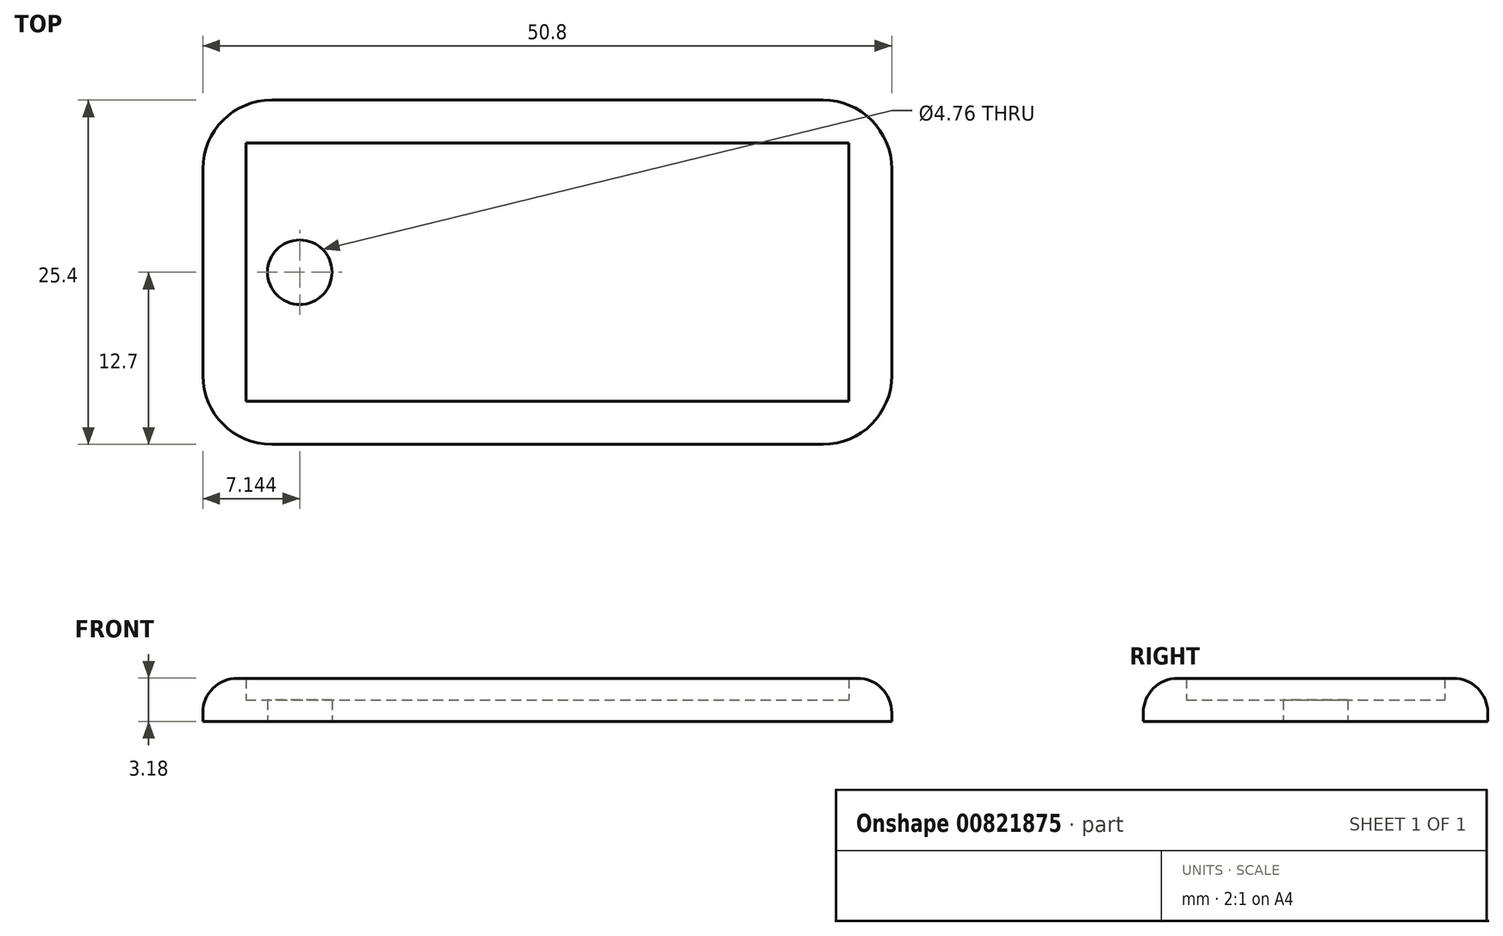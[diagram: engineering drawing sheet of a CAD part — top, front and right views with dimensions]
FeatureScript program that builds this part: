
annotation { "Feature Type Name" : "Feature", "Feature Type Description" : "" }
export const myFeature = defineFeature(function(context is Context, id is Id, definition is map)
    precondition{}
    {
        {
            var Q0;
            Q0=qCreatedBy(makeId("Top.planeOp"),FACE);
            var sketch = newSketch(context, id + "F0", { "sketchPlane" : qUnion([Q0])});
            skLineSegment(sketch, "E0.bottom", {"start": v(0, 0) * mm, "end": v(50.8, 0) * mm});
            skLineSegment(sketch, "E0.top", {"start": v(0, 25.4) * mm, "end": v(50.8, 25.4) * mm});
            skLineSegment(sketch, "E0.left", {"start": v(0, 0) * mm, "end": v(0, 25.4) * mm});
            skLineSegment(sketch, "E0.right", {"start": v(50.8, 0) * mm, "end": v(50.8, 25.4) * mm});
            skPoint(sketch, "E1.centerSnap0", {"position": v(0, 12.7) * mm});
            skLineSegment(sketch, "E2.0", {"start": v(3.18, 3.18) * mm, "end": v(47.63, 3.18) * mm});
            skLineSegment(sketch, "E2.1", {"start": v(3.17, 3.18) * mm, "end": v(3.17, 22.23) * mm});
            skLineSegment(sketch, "E2.2", {"start": v(3.17, 22.23) * mm, "end": v(47.63, 22.23) * mm});
            skLineSegment(sketch, "E2.3", {"start": v(47.63, 3.18) * mm, "end": v(47.63, 22.23) * mm});
            skPoint(sketch, "E1.center.orphan", {"position": v(3.8, 12.7) * mm});
            skCircle(sketch, "E3", {"center": v(7.14, 12.7) * mm, "radius": 2.38 * mm});
            skSolve(sketch);
        }
        {
            var Q0;
            {var subQ4=sQuery(id+"F0.wireOp",EDGE,"E2.0");Q0=makeQuery(id+"F0.imprint","IMPRINT",FACE,{"disambiguationData":[TD([[makeQuery(id+"F0.imprint","IMPRINT",EDGE,{"derivedFrom":subQ4}),1.0]])]});}
            extrude(context, id + "F1", {"entities" : qUnion([Q0]), "depth" : 1.59 * mm, "offsetDistance" : 25.4 * mm});
        }
        {
            var Q0;
            Q0=makeQuery(id+"F0.imprint","IMPRINT",FACE,{"disambiguationData":[TD([[makeQuery(id+"F0.imprint","IMPRINT",EDGE,{"derivedFrom":sQuery(id+"F0.wireOp",EDGE,"E0.bottom")}),1.0]])]});
            extrude(context, id + "F2", {"entities" : qUnion([Q0]), "operationType" : NewBodyOperationType.ADD, "depth" : 3.17 * mm, "offsetDistance" : 25.4 * mm});
        }
        {
            var Q0;
            Q0=makeQuery(id+"F2.opExtrude","SWEPT_EDGE",EDGE,{"disambiguationData":[OSD([sQuery(id+"F0.wireOp",EDGE,"E0.bottom"),sQuery(id+"F0.wireOp",EDGE,"E0.right")])]});
            var Q1;
            Q1=makeQuery(id+"F2.opExtrude","SWEPT_EDGE",EDGE,{"disambiguationData":[OSD([sQuery(id+"F0.wireOp",EDGE,"E0.bottom"),sQuery(id+"F0.wireOp",EDGE,"E0.left")])]});
            var Q2;
            Q2=makeQuery(id+"F2.opExtrude","SWEPT_EDGE",EDGE,{"disambiguationData":[OSD([sQuery(id+"F0.wireOp",EDGE,"E0.top"),sQuery(id+"F0.wireOp",EDGE,"E0.right")])]});
            var Q3;
            Q3=makeQuery(id+"F2.opExtrude","SWEPT_EDGE",EDGE,{"disambiguationData":[OSD([sQuery(id+"F0.wireOp",EDGE,"E0.top"),sQuery(id+"F0.wireOp",EDGE,"E0.left")])]});
            fillet(context, id + "F3", {"entities" : qUnion([Q0, Q1, Q2, Q3]), "radius" : 5.08 * mm, "tangentPropagation" : true, "allowEdgeOverflow" : false});
        }
        {
            var Q0;
            Q0=makeQuery(id+"F2.opExtrude","CAP_EDGE",EDGE,{"disambiguationData":[OSD([sQuery(id+"F0.wireOp",EDGE,"E0.bottom")])],"isStart":false});
            fillet(context, id + "F4", {"entities" : qUnion([Q0]), "radius" : 2.54 * mm, "tangentPropagation" : true, "allowEdgeOverflow" : false});
        }
        {
            var Q0;
            Q0=qCreatedBy(makeId("Top.planeOp"),FACE);
            var sketch = newSketch(context, id + "F5", { "sketchPlane" : qUnion([Q0])});
            skText(sketch, "E4", { "text": "Amanda", "fontName": "OpenSans-Bold.ttf"});
            const initialGuessF5  = {"E4": [0.00918, 0.0093, 1, 0, 0.0066]};
            skSetInitialGuess(sketch, initialGuessF5);
            skSolve(sketch);
        }
        {
            var Q0;
            Q0=qCreatedBy(makeId("Top.planeOp"),FACE);
            var sketch = newSketch(context, id + "F6", { "sketchPlane" : qUnion([Q0])});
            skSolve(sketch);
        }
        {
            var Q0;
            Q0 = qSketchRegion(id + "F6", true);
            var Q1;
            Q1 = qSketchRegion(id + "F5", true);
            extrude(context, id + "F7", {"entities" : qUnion([Q0, Q1]), "operationType" : NewBodyOperationType.ADD, "depth" : 0.8 * mm, "offsetDistance" : 25.4 * mm});
        }
        {
            var Q0;
            Q0 = qSketchRegion(id + "F5", true);
            extrude(context, id + "F8", {"entities" : qUnion([Q0]), "operationType" : NewBodyOperationType.ADD, "depth" : 1 / 812.8 * mm, "offsetDistance" : 25.4 * mm});
        }
        {
            var Q0;
            Q0 = qSketchRegion(id + "F5", true);
            extrude(context, id + "F9", {"entities" : qUnion([Q0]), "operationType" : NewBodyOperationType.ADD, "depth" : 0.8 * mm, "offsetDistance" : 25.4 * mm});
        }
        {
            var Q0;
            Q0 = qSketchRegion(id + "F5", true);
            extrude(context, id + "F10", {"entities" : qUnion([Q0]), "operationType" : NewBodyOperationType.ADD, "depth" : 3 / 812.8 * mm, "offsetDistance" : 25.4 * mm});
        }
    });
